# Revit family: Hager-IC-IP30-Plain_Door-sistema-ES-es
name_source: partatom
category: Electrical Equipment
units: mm (PartAtom-declared; Revit-internal decimal feet)

## family parameters
Cut with Voids When Loaded = No
Host = Face
Panel Configuration = Two Columns, Circuits Across
Part Type = Panelboard
Room Calculation Point = No
Round Connector Dimension = Use Diameter
Shared = No

## types (1)
- Montado superficial IP30 A294 A326.5 P92.5 12 unidad de división - VD212NE
    Default Elevation = 0 mm  [stored 0 ft]
    EF000003 - Tipo de montaje = EV000384 - Montado superficial (escayola)
    EF000007 - Color = EV000202 - Blanco
    EF000008 - Anchura = 294 mm  [stored 0.964567 ft]
    EF000040 - Altura = 326 mm  [stored 1.06955 ft]
    EF000049 - Profundidad = 92 mm  [stored 0.301837 ft]
    EF000116 - Número RAL = 9010
    EF000118 - Con placa de montaje = No
    EF000218 - Profundidad de instalación = 0 mm  [stored 0 ft]
    EF000266 - Número de filas = 2
    EF000332 - Altura de la instalación = 0 mm  [stored 0 ft]
    EF000846 - Anchura de instalación = 0 mm  [stored 0 ft]
    EF001062 - Versión de EMC = No
    EF001088 - Posibilidad de extensión = Yes
    EF001131 - Profundidad interna = 72 mm  [stored 0.23622 ft]
    EF001134 - Carril DIN = Yes
    EF001596 - Material de la carcasa = EV000139 - Plástico
    EF002950 - Anchura de unidades de división = 12
    EF004462 - Tipo de cierre = EV000154 - Otros
    EF005474 - Grado de protección (IP) = EV006410 - IP30
    EF006244 - Tapa/puerta transparente = No
    EF006306 - Con cierre = No
    EF009212 - Versión de la cubierta = EV000116 - Cerrado
    EF015776 - Borne de tierra = No
    EF015777 - Borne neutro = No
    EF015941 - Puerta de transmisión de señal = Yes
    HG000001 - Número de columnas = 1
    HG000002 - Con puerta o tapa = Yes
    HG000003 - Gama = IC
    HG000004 - Referencia del fabricante = VD212NE
    HG000005 - Grosor = 3 mm  [stored 0.00984252 ft]
    HG000006 - Empotrado = No
    HG000007 - Número de columnas vacías = 0
    HG000008 - Número de filas vacías = 0
    HG000009 - Puerta batiente doble = No
    HG000010 - Puertas asimétricas = No
    HG000011 - Filas vacías desde abajo = No
    HG000017 - Distancia entre polos = 18 mm  [stored 0.0590551 ft]
    Manufacturer = Hager
    Model = VD212NE
    Type Comments = IC

note: [stored X ft] marks values corroborated as IEEE doubles in the binary element streams (Revit-internal decimal feet)

## geometry (parser evidence)
native form markers: Sweep x16
no freeform markers — native parametric forms only
